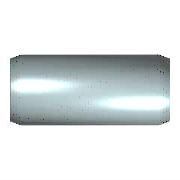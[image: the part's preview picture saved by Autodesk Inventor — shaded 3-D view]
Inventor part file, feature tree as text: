
AUTODESK INVENTOR PART (.ipt)
format: ipt  version: 2023.3 (Build 273359000, 359)  size: 114,688 bytes
history: native  units: mm (DEFAULTED — no unit token found)
features: extrude x1, chamfer x1, sketch x1
ambient origin geometry x8: Origin, YZ Plane, XZ Plane, XY Plane, X Axis, Y Axis, Z Axis, Center Point
bodies: Solid1 (feature_tree)
feature tree (3):
  extrude  "Körper"  Depth=14.0mm
  chamfer  "Skizze2"  [1 undecoded]
  sketch  "Skizze"  dims[d1=2.0mm d2=14.0mm d3=0.0mm d4=0.35mm d5=15.0deg d8=0.35mm d9=15.0deg d11=0.35mm d12=0.35mm d13=0.0mm d15=0.0mm d16=0.0mm]
note: 1 required parameter value undecoded (feature->parameter linkage not recoverable at this tier; creation-order binding heuristic only, values carry confidence <= 0.55)
